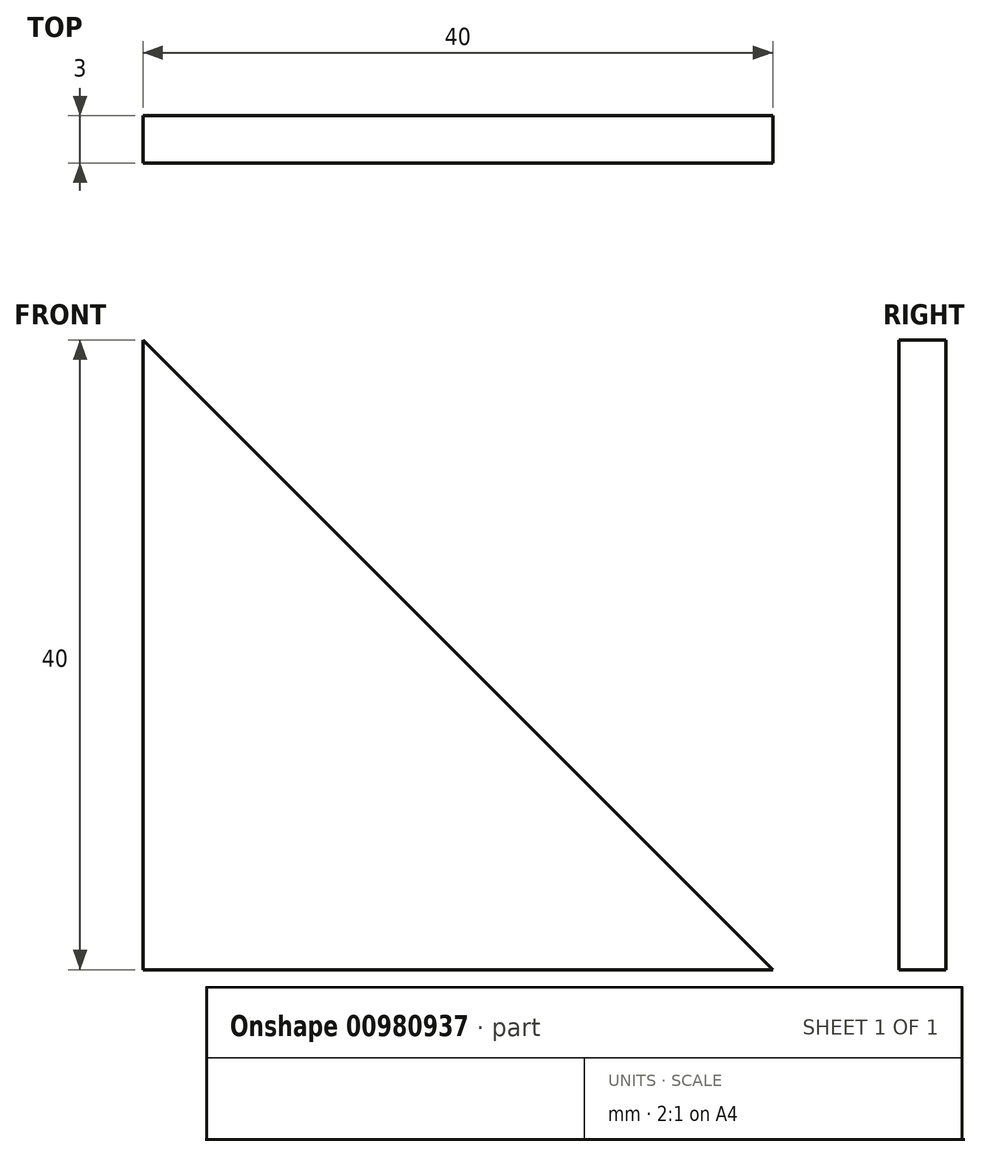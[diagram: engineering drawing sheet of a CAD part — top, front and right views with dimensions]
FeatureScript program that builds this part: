
annotation { "Feature Type Name" : "Feature", "Feature Type Description" : "" }
export const myFeature = defineFeature(function(context is Context, id is Id, definition is map)
    precondition{}
    {
        {
            var Q0;
            Q0=qCreatedBy(makeId("Front.planeOp"),FACE);
            var sketch = newSketch(context, id + "F0", { "sketchPlane" : qUnion([Q0])});
            skLineSegment(sketch, "E0", {"start": v(-13.33, 26.67) * mm, "end": v(-13.33, -13.33) * mm});
            skLineSegment(sketch, "E1", {"start": v(-13.33, -13.33) * mm, "end": v(26.67, -13.33) * mm});
            skLineSegment(sketch, "E2", {"start": v(26.67, -13.33) * mm, "end": v(-13.33, 26.67) * mm});
            skSolve(sketch);
        }
        {
            var Q0;
            Q0=makeQuery(id+"F0.imprint","IMPRINT",FACE,{"disambiguationData":[TD([[makeQuery(id+"F0.imprint","IMPRINT",EDGE,{"derivedFrom":sQuery(id+"F0.wireOp",EDGE,"E0")}),1.0]])]});
            extrude(context, id + "F1", {"entities" : qUnion([Q0]), "depth" : 3 * mm, "offsetDistance" : 25 * mm});
        }
    });
